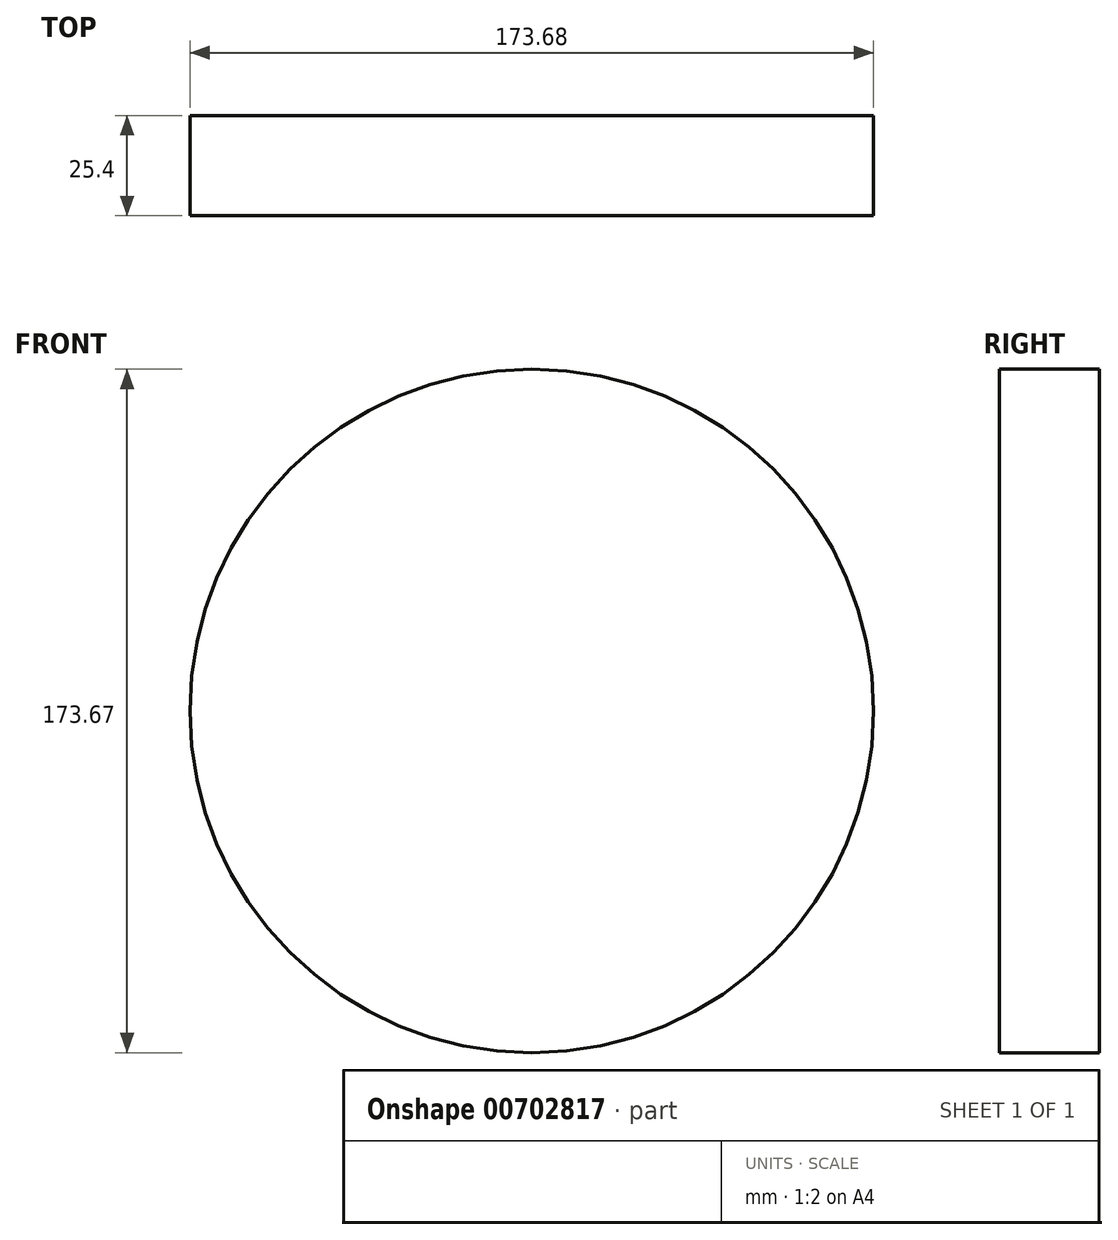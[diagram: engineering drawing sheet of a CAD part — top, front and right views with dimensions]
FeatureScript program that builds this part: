
annotation { "Feature Type Name" : "Feature", "Feature Type Description" : "" }
export const myFeature = defineFeature(function(context is Context, id is Id, definition is map)
    precondition{}
    {
        {
            var Q0;
            Q0=qCreatedBy(makeId("Front.planeOp"),FACE);
            var sketch = newSketch(context, id + "F0", { "sketchPlane" : qUnion([Q0])});
            skCircle(sketch, "E0", {"center": v(-61.24, 61.63) * mm, "radius": 86.84 * mm});
            skSolve(sketch);
        }
        {
            var Q0;
            Q0 = qSketchRegion(id + "F0", true);
            extrude(context, id + "F1", {"entities" : qUnion([Q0]), "depth" : 25.4 * mm, "offsetDistance" : 25.4 * mm});
        }
    });
